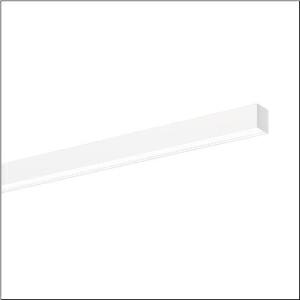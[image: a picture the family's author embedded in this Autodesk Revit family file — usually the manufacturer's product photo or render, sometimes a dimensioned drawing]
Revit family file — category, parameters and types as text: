
# Revit family: silica_r__21_51mx20tct5w_c7ea
name_source: partatom
category: Lighting Fixtures
units: mm (PartAtom-declared; Revit-internal decimal feet)

## family parameters
Cut with Voids When Loaded = No
Host = Face
Light Source = No
Part Type = Normal
Room Calculation Point = No
Round Connector Dimension = Use Diameter
Shared = No

## types (1)
- --- (1 x LED, 6000 lm, 51.3 W, 6500K)
    Apparent Load = 51 VA
    CIE Flux Codes = 48 79 96 100 100
    Color Rendering = 80
    Color Temperature = 6500K
    Default Elevation = 1800 mm
    Description = Silica® 21, office luminaire, primary optical cover: cover, of PMMA, opal, light emission: direct distribution, primary light characteristic: symmetric, installation type: surface-mounted, LED, rated luminous flux: 6.000lm, luminous efficacy: 112lm/W, light colour: 8tw, colour temperature: 2700..6500K, control gear: ECG DALI, with terminal, 3+2-pole, max. 2.5mm², mains connection: 220..240V, AC, 50/60Hz, rated input power: 53.8W, luminaire housing, of aluminium, traffic white (RAL 9016), length: 3.004mm, width: 53mm, height: 53mm, protection rating (complete): IP20, insulation class (complete): insulation class I (protective earthing), certification: CE, permissible operating ambient temperature: 0..+35°C, standard: EN 50419, packaging unit: 1 piece
    Height = 0 mm  [stored 0 ft]
    Lamp = 1 x LED
    Lamp Light Flux = 6000 lm
    Lamp Power = 51.3 W
    Lamp count = 1
    Length = 3004 mm
    Luminous efficacy = 117 lm/W
    Manufacturer = Siteco
    ModVariant = No
    Model = 51MX20TCT5W
    Mounting Place = Ceiling
    Mounting Type = Recessed
    Number of Poles = 1
    OnlyDefault = Yes
    Power Factor = 1
    Product Name = Silica® 21
    Product group = office luminaire | ceiling recessed
    ProductGroupID = 400
    Protection Class = Protection class I
    Protection Degree = IP 20
    RLX_Detail_Level = 1
    RLX_Emergency_Light_Flux = 0 lm
    RLX_Emergency_Type = 0
    RLX_Emergency_Type_DB = No
    RlxData = <blob elided: 20605 chars, md5=fea4fbb8>
    Socket = socket
    Standby Power = 0 W
    System Light Flux = 6000 lm
    System Power = 51 W
    Type Comments = individual setting
    Type Image = l_1335877.jpg
    URL = http://relux.com
    VarID = @adj_109501
    Voltage = 0 V
    Weight = 0.00 kg
    Width = 53 mm

note: [stored X ft] marks values corroborated as IEEE doubles in the binary element streams (Revit-internal decimal feet)

## geometry (parser evidence)
native form markers: Blend x4, Sweep x10
no freeform markers — native parametric forms only
